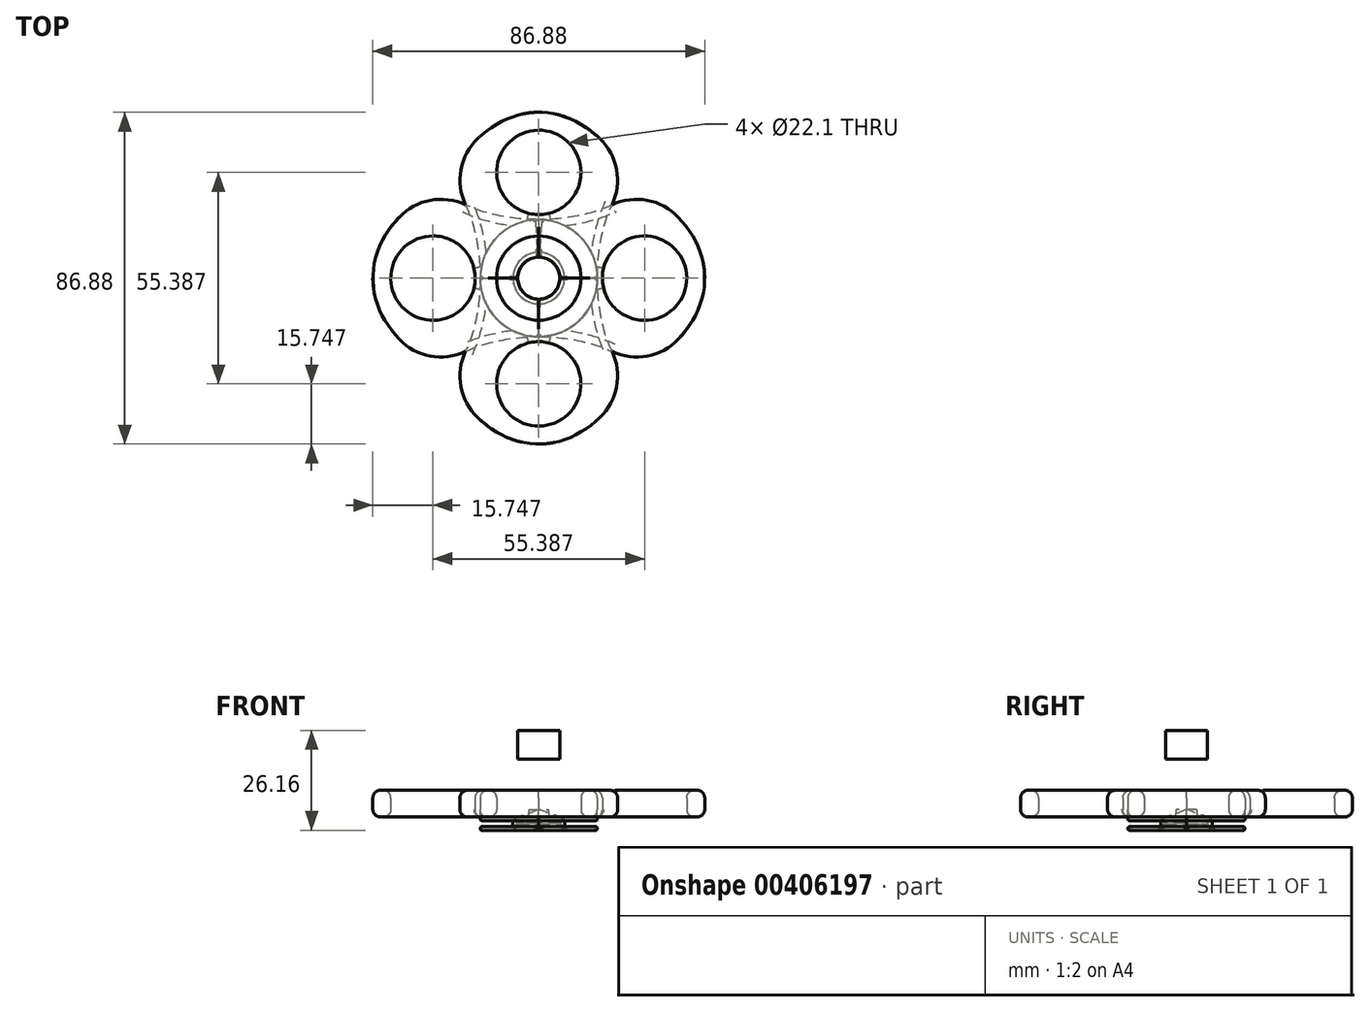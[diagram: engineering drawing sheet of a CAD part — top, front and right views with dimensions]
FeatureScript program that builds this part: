
annotation { "Feature Type Name" : "Feature", "Feature Type Description" : "" }
export const myFeature = defineFeature(function(context is Context, id is Id, definition is map)
    precondition{}
    {
        {
            var Q0;
            Q0=qCreatedBy(makeId("Top.planeOp"),FACE);
            var sketch = newSketch(context, id + "F0", { "sketchPlane" : qUnion([Q0])});
            skCircle(sketch, "E0", {"center": v(0, 0) * mm, "radius": 11.05 * mm});
            skEllipse(sketch, "E1", {"center": v(0, 0) * mm, "majorRadius": 43.44 * mm, "minorRadius": 29.52 * mm, "majorAxis": v(0, 1)});
            skEllipse(sketch, "E2", {"center": v(29.52, 0) * mm, "majorRadius": 28 * mm, "minorRadius": 14.19 * mm, "majorAxis": v(0, -1)});
            skLineSegment(sketch, "E3", {"start": v(0, 58.33) * mm, "end": v(0, -59.11) * mm});
            skEllipse(sketch, "E4", {"center": v(-29.52, 0) * mm, "majorRadius": 27.94 * mm, "minorRadius": 14.94 * mm, "majorAxis": v(0, 1)});
            skCircle(sketch, "E5", {"center": v(0, 27.7) * mm, "radius": 11.05 * mm});
            skLineSegment(sketch, "E6", {"start": v(54.05, 0) * mm, "end": v(-64.12, 0) * mm});
            skCircle(sketch, "E7", {"center": v(0, 0) * mm, "radius": 5.5 * mm});
            skCircle(sketch, "E8", {"center": v(0, 0) * mm, "radius": 15.34 * mm});
            skCircle(sketch, "E9", {"center": v(0, 0) * mm, "radius": 6.75 * mm});
            skSolve(sketch);
        }
        {
            var Q0;
            {var subQ1=sQuery(id+"F0.wireOp",EDGE,"E3");var subQ5=sQuery(id+"F0.wireOp",EDGE,"E0");var subQ6=makeQuery(id+"F0.imprint","INTERSECT",VERTEX,{"disambiguationData":[OD(0.0)],"derivedFrom":[subQ5,subQ1]});Q0=makeQuery(id+"F0.imprint","IMPRINT",FACE,{"disambiguationData":[TD([[makeQuery(id+"F0.imprint","IMPRINT",EDGE,{"disambiguationData":[TD([[subQ6,1.0]])],"derivedFrom":subQ5}),-1.0]])]});}
            var Q1;
            {var subQ1=sQuery(id+"F0.wireOp",EDGE,"E3");var subQ6=sQuery(id+"F0.wireOp",EDGE,"E1");var subQ9=makeQuery(id+"F0.imprint","INTERSECT",VERTEX,{"disambiguationData":[OD(0.0)],"derivedFrom":[subQ6,subQ1]});Q1=makeQuery(id+"F0.imprint","IMPRINT",FACE,{"disambiguationData":[TD([[makeQuery(id+"F0.imprint","IMPRINT",EDGE,{"disambiguationData":[TD([[subQ9,1.0]])],"derivedFrom":subQ6}),1.0]])]});}
            extrude(context, id + "F1", {"entities" : qUnion([Q0, Q1]), "depth" : 7 * mm});
        }
        {
            var Q0;
            {var subQ0=sQuery(id+"F0.wireOp",EDGE,"E3");var subQ1=sQuery(id+"F0.wireOp",EDGE,"E0");var subQ2=makeQuery(id+"F0.imprint","INTERSECT",VERTEX,{"disambiguationData":[OD(0.0)],"derivedFrom":[subQ1,subQ0]});Q0=makeQuery(id+"F0.imprint","IMPRINT",FACE,{"disambiguationData":[TD([[makeQuery(id+"F0.imprint","IMPRINT",EDGE,{"disambiguationData":[TD([[subQ2,1.0]])],"derivedFrom":subQ1}),-1.0]])]});}
            var Q1;
            {var subQ0=sQuery(id+"F0.wireOp",EDGE,"E3");var subQ1=sQuery(id+"F0.wireOp",EDGE,"E0");var subQ2=makeQuery(id+"F0.imprint","INTERSECT",VERTEX,{"disambiguationData":[OD(0.0)],"derivedFrom":[subQ1,subQ0]});Q1=makeQuery(id+"F0.imprint","IMPRINT",FACE,{"disambiguationData":[TD([[makeQuery(id+"F0.imprint","IMPRINT",EDGE,{"disambiguationData":[TD([[subQ2,1.0]])],"derivedFrom":subQ1}),1.0]])]});}
            var Q2;
            {var subQ0=sQuery(id+"F0.wireOp",EDGE,"E9");var subQ1=sQuery(id+"F0.wireOp",EDGE,"E3");var subQ2=makeQuery(id+"F0.imprint","INTERSECT",VERTEX,{"disambiguationData":[OD(0.0)],"derivedFrom":[subQ1,subQ0]});Q2=makeQuery(id+"F0.imprint","IMPRINT",FACE,{"disambiguationData":[TD([[makeQuery(id+"F0.imprint","IMPRINT",EDGE,{"disambiguationData":[TD([[subQ2,-1.0]])],"derivedFrom":subQ1}),1.0]])]});}
            extrude(context, id + "F2", {"entities" : qUnion([Q0, Q1, Q2]), "operationType" : NewBodyOperationType.ADD, "oppositeDirection" : true, "depth" : 1 * mm});
        }
        {
            var Q0;
            {var subQ0=sQuery(id+"F0.wireOp",EDGE,"E9");var subQ1=sQuery(id+"F0.wireOp",EDGE,"E3");var subQ2=makeQuery(id+"F0.imprint","INTERSECT",VERTEX,{"disambiguationData":[OD(0.0)],"derivedFrom":[subQ1,subQ0]});Q0=makeQuery(id+"F0.imprint","IMPRINT",FACE,{"disambiguationData":[TD([[makeQuery(id+"F0.imprint","IMPRINT",EDGE,{"disambiguationData":[TD([[subQ2,-1.0]])],"derivedFrom":subQ1}),1.0]])]});}
            extrude(context, id + "F3", {"entities" : qUnion([Q0]), "operationType" : NewBodyOperationType.ADD, "oppositeDirection" : true, "depth" : 2.5 * mm});
        }
        {
            var Q0;
            {var subQ0=sQuery(id+"F0.wireOp",EDGE,"E9");var subQ1=sQuery(id+"F0.wireOp",EDGE,"E3");var subQ2=makeQuery(id+"F0.imprint","INTERSECT",VERTEX,{"disambiguationData":[OD(0.0)],"derivedFrom":[subQ1,subQ0]});Q0=makeQuery(id+"F0.imprint","IMPRINT",FACE,{"disambiguationData":[TD([[makeQuery(id+"F0.imprint","IMPRINT",EDGE,{"disambiguationData":[TD([[subQ2,-1.0]])],"derivedFrom":subQ1}),1.0]])]});}
            var Q1;
            {var subQ0=sQuery(id+"F0.wireOp",EDGE,"E3");var subQ1=sQuery(id+"F0.wireOp",EDGE,"E0");var subQ2=makeQuery(id+"F0.imprint","INTERSECT",VERTEX,{"disambiguationData":[OD(0.0)],"derivedFrom":[subQ1,subQ0]});Q1=makeQuery(id+"F0.imprint","IMPRINT",FACE,{"disambiguationData":[TD([[makeQuery(id+"F0.imprint","IMPRINT",EDGE,{"disambiguationData":[TD([[subQ2,1.0]])],"derivedFrom":subQ1}),1.0]])]});}
            var Q2;
            {var subQ0=sQuery(id+"F0.wireOp",EDGE,"E3");var subQ1=sQuery(id+"F0.wireOp",EDGE,"E0");var subQ2=makeQuery(id+"F0.imprint","INTERSECT",VERTEX,{"disambiguationData":[OD(0.0)],"derivedFrom":[subQ1,subQ0]});Q2=makeQuery(id+"F0.imprint","IMPRINT",FACE,{"disambiguationData":[TD([[makeQuery(id+"F0.imprint","IMPRINT",EDGE,{"disambiguationData":[TD([[subQ2,1.0]])],"derivedFrom":subQ1}),-1.0]])]});}
            extrude(context, id + "F4", {"entities" : qUnion([Q0, Q1, Q2]), "operationType" : NewBodyOperationType.ADD, "oppositeDirection" : true, "depth" : 3.5 * mm, "hasSecondDirection" : true, "secondDirectionOppositeDirection" : true, "secondDirectionDepth" : 2.5 * mm});
        }
        {
            var Q0;
            Q0=makeQuery(id+"F1.opExtrude","SWEPT_BODY",BODY,{"disambiguationData":[OSD([sQuery(id+"F0.wireOp",EDGE,"E0"),sQuery(id+"F0.wireOp",EDGE,"E1"),sQuery(id+"F0.wireOp",EDGE,"E2"),sQuery(id+"F0.wireOp",EDGE,"E3"),sQuery(id+"F0.wireOp",EDGE,"E5"),sQuery(id+"F0.wireOp",EDGE,"E6")])]});
            var Q1;
            Q1=qCreatedBy(makeId("Right.planeOp"),FACE);
            mirror(context, id + "F5", {"operationType" : NewBodyOperationType.ADD, "entities" : qUnion([Q0]), "mirrorPlane" : qUnion([Q1])});
        }
        {
            var Q0;
            {var subQ0=sQuery(id+"F0.wireOp",EDGE,"E6");var subQ1=sQuery(id+"F0.wireOp",EDGE,"E3");var subQ2=makeQuery(id+"F0.imprint","INTERSECT",VERTEX,{"derivedFrom":[subQ1,subQ0]});Q0=makeQuery(id+"F0.imprint","IMPRINT",FACE,{"disambiguationData":[TD([[makeQuery(id+"F0.imprint","IMPRINT",EDGE,{"disambiguationData":[TD([[subQ2,-1.0]])],"derivedFrom":subQ1}),-1.0]])]});}
            var Q1;
            {var subQ0=sQuery(id+"F0.wireOp",EDGE,"E7");var subQ1=sQuery(id+"F0.wireOp",EDGE,"E3");var subQ2=makeQuery(id+"F0.imprint","INTERSECT",VERTEX,{"disambiguationData":[OD(0.0)],"derivedFrom":[subQ1,subQ0]});Q1=makeQuery(id+"F0.imprint","IMPRINT",FACE,{"disambiguationData":[TD([[makeQuery(id+"F0.imprint","IMPRINT",EDGE,{"disambiguationData":[TD([[subQ2,-1.0]])],"derivedFrom":subQ1}),-1.0]])]});}
            var Q2;
            {var subQ0=sQuery(id+"F0.wireOp",EDGE,"E7");var subQ1=sQuery(id+"F0.wireOp",EDGE,"E3");var subQ2=makeQuery(id+"F0.imprint","INTERSECT",VERTEX,{"disambiguationData":[OD(0.0)],"derivedFrom":[subQ1,subQ0]});Q2=makeQuery(id+"F0.imprint","IMPRINT",FACE,{"disambiguationData":[TD([[makeQuery(id+"F0.imprint","IMPRINT",EDGE,{"disambiguationData":[TD([[subQ2,-1.0]])],"derivedFrom":subQ1}),1.0]])]});}
            var Q3;
            {var subQ0=sQuery(id+"F0.wireOp",EDGE,"E6");var subQ1=sQuery(id+"F0.wireOp",EDGE,"E3");var subQ2=makeQuery(id+"F0.imprint","INTERSECT",VERTEX,{"derivedFrom":[subQ1,subQ0]});Q3=makeQuery(id+"F0.imprint","IMPRINT",FACE,{"disambiguationData":[TD([[makeQuery(id+"F0.imprint","IMPRINT",EDGE,{"disambiguationData":[TD([[subQ2,-1.0]])],"derivedFrom":subQ1}),1.0]])]});}
            extrude(context, id + "F6", {"entities" : qUnion([Q0, Q1, Q2, Q3]), "depth" : 22.66 * mm, "hasSecondDirection" : true, "secondDirectionOppositeDirection" : false, "secondDirectionDepth" : 15.2 * mm});
        }
        {
            var Q0;
            {var subQ0=makeQuery(id+"F4.opExtrude","CAP_FACE",FACE,{"disambiguationData":[OSD([sQuery(id+"F0.wireOp",EDGE,"E3"),sQuery(id+"F0.wireOp",EDGE,"E6"),sQuery(id+"F0.wireOp",EDGE,"E7"),sQuery(id+"F0.wireOp",EDGE,"E8")])],"isStart":false});Q0=makeQuery(id+"F5.boolean.opBoolean","MERGE",FACE,{"derivedFrom":[subQ0,makeQuery(id+"F5.opPattern","COPY",FACE,{"derivedFrom":subQ0,"instanceName":"1"})]});}
            var sketch = newSketch(context, id + "F7", { "sketchPlane" : qUnion([Q0])});
            skLineSegment(sketch, "E10", {"start": v(0, -18) * mm, "end": v(-1, -18) * mm});
            skLineSegment(sketch, "E11", {"start": v(-1, -18) * mm, "end": v(0, 0) * mm});
            skLineSegment(sketch, "E12", {"start": v(0, 0) * mm, "end": v(1, -18) * mm});
            skLineSegment(sketch, "E13", {"start": v(1, -18) * mm, "end": v(0, -18) * mm});
            skSolve(sketch);
        }
        {
            var Q0;
            {var subQ0=makeQuery(id+"F1.opExtrude","CAP_EDGE",EDGE,{"disambiguationData":[OSD([sQuery(id+"F0.wireOp",EDGE,"E5")])],"isStart":true});Q0=makeQuery(id+"F5.boolean.opBoolean","MERGE",EDGE,{"derivedFrom":[subQ0,makeQuery(id+"F5.opPattern","COPY",EDGE,{"derivedFrom":subQ0,"instanceName":"1"})]});}
            var Q1;
            Q1=makeQuery(id+"F1.opExtrude","CAP_EDGE",EDGE,{"disambiguationData":[OSD([sQuery(id+"F0.wireOp",EDGE,"E2")])],"isStart":true});
            var Q2;
            Q2=makeQuery(id+"F1.opExtrude","CAP_EDGE",EDGE,{"disambiguationData":[OSD([sQuery(id+"F0.wireOp",EDGE,"E2")])],"isStart":false});
            var Q3;
            Q3=makeQuery(id+"F5.opPattern","COPY",EDGE,{"derivedFrom":makeQuery(id+"F1.opExtrude","CAP_EDGE",EDGE,{"disambiguationData":[OSD([sQuery(id+"F0.wireOp",EDGE,"E2")])],"isStart":true}),"instanceName":"1"});
            var Q4;
            {var subQ0=makeQuery(id+"F1.opExtrude","CAP_EDGE",EDGE,{"disambiguationData":[OSD([sQuery(id+"F0.wireOp",EDGE,"E1")])],"isStart":true});Q4=makeQuery(id+"F5.boolean.opBoolean","MERGE",EDGE,{"derivedFrom":[subQ0,makeQuery(id+"F5.opPattern","COPY",EDGE,{"derivedFrom":subQ0,"instanceName":"1"})]});}
            var Q5;
            {var subQ0=makeQuery(id+"F4.opExtrude","CAP_EDGE",EDGE,{"disambiguationData":[OSD([sQuery(id+"F0.wireOp",EDGE,"E7")])],"isStart":false});Q5=makeQuery(id+"F5.boolean.opBoolean","MERGE",EDGE,{"derivedFrom":[subQ0,makeQuery(id+"F5.opPattern","COPY",EDGE,{"derivedFrom":subQ0,"instanceName":"1"})]});}
            var Q6;
            {var subQ0=makeQuery(id+"F2.opExtrude","CAP_EDGE",EDGE,{"disambiguationData":[OSD([sQuery(id+"F0.wireOp",EDGE,"E7")])],"isStart":true});Q6=makeQuery(id+"F5.boolean.opBoolean","MERGE",EDGE,{"derivedFrom":[subQ0,makeQuery(id+"F5.opPattern","COPY",EDGE,{"derivedFrom":subQ0,"instanceName":"1"})]});}
            var Q7;
            {var subQ0=makeQuery(id+"F1.opExtrude","CAP_EDGE",EDGE,{"disambiguationData":[OSD([sQuery(id+"F0.wireOp",EDGE,"E1")])],"isStart":false});Q7=makeQuery(id+"F5.boolean.opBoolean","MERGE",EDGE,{"derivedFrom":[subQ0,makeQuery(id+"F5.opPattern","COPY",EDGE,{"derivedFrom":subQ0,"instanceName":"1"})]});}
            var Q8;
            {var subQ0=makeQuery(id+"F1.opExtrude","CAP_EDGE",EDGE,{"disambiguationData":[OSD([sQuery(id+"F0.wireOp",EDGE,"E5")])],"isStart":false});Q8=makeQuery(id+"F5.boolean.opBoolean","MERGE",EDGE,{"derivedFrom":[subQ0,makeQuery(id+"F5.opPattern","COPY",EDGE,{"derivedFrom":subQ0,"instanceName":"1"})]});}
            var Q9;
            {var subQ0=makeQuery(id+"F1.opExtrude","CAP_EDGE",EDGE,{"disambiguationData":[OSD([sQuery(id+"F0.wireOp",EDGE,"E0")])],"isStart":false});Q9=makeQuery(id+"F5.boolean.opBoolean","MERGE",EDGE,{"derivedFrom":[subQ0,makeQuery(id+"F5.opPattern","COPY",EDGE,{"derivedFrom":subQ0,"instanceName":"1"})]});}
            var Q10;
            Q10=makeQuery(id+"F5.opPattern","COPY",EDGE,{"derivedFrom":makeQuery(id+"F1.opExtrude","CAP_EDGE",EDGE,{"disambiguationData":[OSD([sQuery(id+"F0.wireOp",EDGE,"E2")])],"isStart":false}),"instanceName":"1"});
            fillet(context, id + "F8", {"entities" : qUnion([Q0, Q1, Q2, Q3, Q4, Q5, Q6, Q7, Q8, Q9, Q10]), "radius" : 2 * mm, "tangentPropagation" : true, "allowEdgeOverflow" : false});
        }
        {
            var Q0;
            Q0=makeQuery(id+"F5.opPattern","COPY",EDGE,{"derivedFrom":makeQuery(id+"F1.opExtrude","SWEPT_EDGE",EDGE,{"disambiguationData":[OSD([sQuery(id+"F0.wireOp",EDGE,"E1"),sQuery(id+"F0.wireOp",EDGE,"E2")])]}),"instanceName":"1"});
            var Q1;
            Q1=makeQuery(id+"F1.opExtrude","SWEPT_EDGE",EDGE,{"disambiguationData":[OSD([sQuery(id+"F0.wireOp",EDGE,"E1"),sQuery(id+"F0.wireOp",EDGE,"E2")])]});
            fillet(context, id + "F9", {"entities" : qUnion([Q0, Q1]), "radius" : 15 * mm, "tangentPropagation" : true, "allowEdgeOverflow" : false});
        }
        {
            var Q0;
            {var subQ0=makeQuery(id+"F4.opExtrude","CAP_EDGE",EDGE,{"disambiguationData":[OSD([sQuery(id+"F0.wireOp",EDGE,"E8")])],"isStart":false});Q0=makeQuery(id+"F5.boolean.opBoolean","MERGE",EDGE,{"derivedFrom":[subQ0,makeQuery(id+"F5.opPattern","COPY",EDGE,{"derivedFrom":subQ0,"instanceName":"1"})]});}
            var Q1;
            {var subQ0=makeQuery(id+"F2.opExtrude","CAP_EDGE",EDGE,{"disambiguationData":[OSD([sQuery(id+"F0.wireOp",EDGE,"E8")])],"isStart":false});Q1=makeQuery(id+"F5.boolean.opBoolean","MERGE",EDGE,{"derivedFrom":[subQ0,makeQuery(id+"F5.opPattern","COPY",EDGE,{"derivedFrom":subQ0,"instanceName":"1"})]});}
            var Q2;
            {var subQ0=makeQuery(id+"F4.opExtrude","CAP_EDGE",EDGE,{"disambiguationData":[OSD([sQuery(id+"F0.wireOp",EDGE,"E8")])],"isStart":true});Q2=makeQuery(id+"F5.boolean.opBoolean","MERGE",EDGE,{"derivedFrom":[subQ0,makeQuery(id+"F5.opPattern","COPY",EDGE,{"derivedFrom":subQ0,"instanceName":"1"})]});}
            var Q3;
            {var subQ0=makeQuery(id+"F2.opExtrude","CAP_EDGE",EDGE,{"disambiguationData":[OSD([sQuery(id+"F0.wireOp",EDGE,"E8")])],"isStart":true});Q3=makeQuery(id+"F5.boolean.opBoolean","MERGE",EDGE,{"derivedFrom":[subQ0,makeQuery(id+"F5.opPattern","COPY",EDGE,{"derivedFrom":subQ0,"instanceName":"1"})]});}
            var Q4;
            {var subQ0=makeQuery(id+"F2.opExtrude","CAP_EDGE",EDGE,{"disambiguationData":[OSD([sQuery(id+"F0.wireOp",EDGE,"E8")])],"isStart":true});Q4=makeQuery(id+"F5.boolean.opBoolean","MERGE",EDGE,{"derivedFrom":[subQ0,makeQuery(id+"F5.opPattern","COPY",EDGE,{"derivedFrom":subQ0,"instanceName":"1"})]});}
            fillet(context, id + "F10", {"entities" : qUnion([Q0, Q1, Q2, Q3, Q4]), "radius" : 0.5 * mm, "tangentPropagation" : true, "allowEdgeOverflow" : false});
        }
        {
            var Q0;
            Q0=makeQuery(id+"F1.opExtrude","SWEPT_BODY",BODY,{"disambiguationData":[OSD([sQuery(id+"F0.wireOp",EDGE,"E0"),sQuery(id+"F0.wireOp",EDGE,"E1"),sQuery(id+"F0.wireOp",EDGE,"E2"),sQuery(id+"F0.wireOp",EDGE,"E3"),sQuery(id+"F0.wireOp",EDGE,"E5"),sQuery(id+"F0.wireOp",EDGE,"E6")])]});
            var Q1;
            Q1=makeQuery(id+"F6.opExtrude","CAP_EDGE",EDGE,{"disambiguationData":[OSD([sQuery(id+"F0.wireOp",EDGE,"E7")])],"isStart":true});
            circularPattern(context, id + "F11", {"operationType" : NewBodyOperationType.ADD, "entities" : qUnion([Q0]), "axis" : qUnion([Q1]), "angle" : 360 * degree, "instanceCount" : 4, "equalSpace" : true});
        }
        {
            var Q0;
            {var subQ0=sQuery(id+"F7.wireOp",EDGE,"E11");var subQ1=makeQuery(id+"F4.opExtrude","CAP_EDGE",EDGE,{"disambiguationData":[OSD([sQuery(id+"F0.wireOp",EDGE,"E8")])],"isStart":false});var subQ2=makeQuery(id+"F5.boolean.opBoolean","MERGE",EDGE,{"derivedFrom":[subQ1,makeQuery(id+"F5.opPattern","COPY",EDGE,{"derivedFrom":subQ1,"instanceName":"1"})]});var subQ3=makeQuery(id+"F7.imprint","INTERSECT",VERTEX,{"derivedFrom":[subQ2,subQ0]});Q0=makeQuery(id+"F7.imprint","IMPRINT",FACE,{"disambiguationData":[TD([[makeQuery(id+"F7.imprint","IMPRINT",EDGE,{"disambiguationData":[TD([[subQ3,-1.0]])],"derivedFrom":subQ0}),-1.0]])]});}
            extrude(context, id + "F12", {"entities" : qUnion([Q0]), "operationType" : NewBodyOperationType.REMOVE, "oppositeDirection" : true, "depth" : 1 * mm});
        }
        {
            var Q0;
            {var subQ0=sQuery(id+"F0.wireOp",EDGE,"E8");var subQ3=sQuery(id+"F0.wireOp",EDGE,"E7");var subQ6=makeQuery(id+"F4.opExtrude","CAP_FACE",FACE,{"disambiguationData":[OSD([sQuery(id+"F0.wireOp",EDGE,"E3"),sQuery(id+"F0.wireOp",EDGE,"E6"),subQ3,subQ0])],"isStart":false});var subQ7=makeQuery(id+"F5.boolean.opBoolean","MERGE",FACE,{"derivedFrom":[subQ6,makeQuery(id+"F5.opPattern","COPY",FACE,{"derivedFrom":subQ6,"instanceName":"1"})]});Q0=makeQuery(id+"FEYc9VW4fI0q4IH_2.1.F12.boolean.opBoolean","SPLIT",FACE,{"disambiguationData":[TD([makeQuery(id+"F12.boolean.opBoolean","COPY",FACE,{"derivedFrom":makeQuery(id+"F12.opExtrude","SWEPT_FACE",FACE,{"disambiguationData":[OSD([sQuery(id+"F7.wireOp",EDGE,"E12")])]})})])],"derivedFrom":makeQuery(id+"F11.boolean.opBoolean","MERGE",FACE,{"derivedFrom":[subQ7,makeQuery(id+"F11.opPattern","COPY",FACE,{"derivedFrom":subQ7,"instanceName":"1"}),makeQuery(id+"F11.opPattern","COPY",FACE,{"derivedFrom":subQ7,"instanceName":"2"}),makeQuery(id+"F11.opPattern","COPY",FACE,{"derivedFrom":subQ7,"instanceName":"3"})]})});}
            var Q1;
            {var subQ0=sQuery(id+"F0.wireOp",EDGE,"E8");var subQ6=sQuery(id+"F0.wireOp",EDGE,"E7");var subQ12=makeQuery(id+"FEYc9VW4fI0q4IH_2.1.F12.opExtrude","SWEPT_FACE",FACE,{"disambiguationData":[OSD([sQuery(id+"F7.wireOp",EDGE,"E12")])]});var subQ13=sQuery(id+"F7.wireOp",EDGE,"E11");var subQ14=makeQuery(id+"F4.opExtrude","CAP_FACE",FACE,{"disambiguationData":[OSD([sQuery(id+"F0.wireOp",EDGE,"E3"),sQuery(id+"F0.wireOp",EDGE,"E6"),subQ6,subQ0])],"isStart":false});var subQ15=makeQuery(id+"F5.boolean.opBoolean","MERGE",FACE,{"derivedFrom":[subQ14,makeQuery(id+"F5.opPattern","COPY",FACE,{"derivedFrom":subQ14,"instanceName":"1"})]});Q1=makeQuery(id+"FEYc9VW4fI0q4IH_2.2.F12.boolean.opBoolean","SPLIT",FACE,{"disambiguationData":[TD([makeQuery(id+"FEYc9VW4fI0q4IH_2.1.F12.boolean.opBoolean","COPY",FACE,{"derivedFrom":subQ12})])],"derivedFrom":makeQuery(id+"FEYc9VW4fI0q4IH_2.1.F12.boolean.opBoolean","SPLIT",FACE,{"disambiguationData":[TD([makeQuery(id+"F12.boolean.opBoolean","COPY",FACE,{"derivedFrom":makeQuery(id+"F12.opExtrude","SWEPT_FACE",FACE,{"disambiguationData":[OSD([subQ13])]})})])],"derivedFrom":makeQuery(id+"F11.boolean.opBoolean","MERGE",FACE,{"derivedFrom":[subQ15,makeQuery(id+"F11.opPattern","COPY",FACE,{"derivedFrom":subQ15,"instanceName":"1"}),makeQuery(id+"F11.opPattern","COPY",FACE,{"derivedFrom":subQ15,"instanceName":"2"}),makeQuery(id+"F11.opPattern","COPY",FACE,{"derivedFrom":subQ15,"instanceName":"3"})]})})});}
            var Q2;
            {var subQ0=sQuery(id+"F0.wireOp",EDGE,"E8");var subQ6=sQuery(id+"F7.wireOp",EDGE,"E12");var subQ7=makeQuery(id+"FEYc9VW4fI0q4IH_2.2.F12.opExtrude","SWEPT_FACE",FACE,{"disambiguationData":[OSD([subQ6])]});var subQ8=sQuery(id+"F0.wireOp",EDGE,"E7");var subQ14=sQuery(id+"F7.wireOp",EDGE,"E11");var subQ15=makeQuery(id+"F12.boolean.opBoolean","COPY",FACE,{"derivedFrom":makeQuery(id+"F12.opExtrude","SWEPT_FACE",FACE,{"disambiguationData":[OSD([subQ14])]})});var subQ16=makeQuery(id+"F4.opExtrude","CAP_FACE",FACE,{"disambiguationData":[OSD([sQuery(id+"F0.wireOp",EDGE,"E3"),sQuery(id+"F0.wireOp",EDGE,"E6"),subQ8,subQ0])],"isStart":false});var subQ17=makeQuery(id+"F5.boolean.opBoolean","MERGE",FACE,{"derivedFrom":[subQ16,makeQuery(id+"F5.opPattern","COPY",FACE,{"derivedFrom":subQ16,"instanceName":"1"})]});Q2=makeQuery(id+"FEYc9VW4fI0q4IH_2.3.F12.boolean.opBoolean","SPLIT",FACE,{"disambiguationData":[TD([makeQuery(id+"FEYc9VW4fI0q4IH_2.2.F12.boolean.opBoolean","COPY",FACE,{"derivedFrom":subQ7})])],"derivedFrom":makeQuery(id+"FEYc9VW4fI0q4IH_2.2.F12.boolean.opBoolean","SPLIT",FACE,{"disambiguationData":[TD([subQ15])],"derivedFrom":makeQuery(id+"FEYc9VW4fI0q4IH_2.1.F12.boolean.opBoolean","SPLIT",FACE,{"disambiguationData":[TD([subQ15])],"derivedFrom":makeQuery(id+"F11.boolean.opBoolean","MERGE",FACE,{"derivedFrom":[subQ17,makeQuery(id+"F11.opPattern","COPY",FACE,{"derivedFrom":subQ17,"instanceName":"1"}),makeQuery(id+"F11.opPattern","COPY",FACE,{"derivedFrom":subQ17,"instanceName":"2"}),makeQuery(id+"F11.opPattern","COPY",FACE,{"derivedFrom":subQ17,"instanceName":"3"})]})})})});}
            var Q3;
            {var subQ0=sQuery(id+"F0.wireOp",EDGE,"E8");var subQ6=makeQuery(id+"F12.boolean.opBoolean","COPY",FACE,{"derivedFrom":makeQuery(id+"F12.opExtrude","SWEPT_FACE",FACE,{"disambiguationData":[OSD([sQuery(id+"F7.wireOp",EDGE,"E11")])]})});var subQ7=sQuery(id+"F0.wireOp",EDGE,"E7");var subQ14=makeQuery(id+"F4.opExtrude","CAP_FACE",FACE,{"disambiguationData":[OSD([sQuery(id+"F0.wireOp",EDGE,"E3"),sQuery(id+"F0.wireOp",EDGE,"E6"),subQ7,subQ0])],"isStart":false});var subQ15=makeQuery(id+"F5.boolean.opBoolean","MERGE",FACE,{"derivedFrom":[subQ14,makeQuery(id+"F5.opPattern","COPY",FACE,{"derivedFrom":subQ14,"instanceName":"1"})]});Q3=makeQuery(id+"FEYc9VW4fI0q4IH_2.3.F12.boolean.opBoolean","SPLIT",FACE,{"disambiguationData":[TD([subQ6])],"derivedFrom":makeQuery(id+"FEYc9VW4fI0q4IH_2.2.F12.boolean.opBoolean","SPLIT",FACE,{"disambiguationData":[TD([subQ6])],"derivedFrom":makeQuery(id+"FEYc9VW4fI0q4IH_2.1.F12.boolean.opBoolean","SPLIT",FACE,{"disambiguationData":[TD([subQ6])],"derivedFrom":makeQuery(id+"F11.boolean.opBoolean","MERGE",FACE,{"derivedFrom":[subQ15,makeQuery(id+"F11.opPattern","COPY",FACE,{"derivedFrom":subQ15,"instanceName":"1"}),makeQuery(id+"F11.opPattern","COPY",FACE,{"derivedFrom":subQ15,"instanceName":"2"}),makeQuery(id+"F11.opPattern","COPY",FACE,{"derivedFrom":subQ15,"instanceName":"3"})]})})})});}
            fillet(context, id + "F13", {"entities" : qUnion([Q0, Q1, Q2, Q3]), "radius" : 0.4 * mm, "tangentPropagation" : true, "allowEdgeOverflow" : false});
        }
    });
